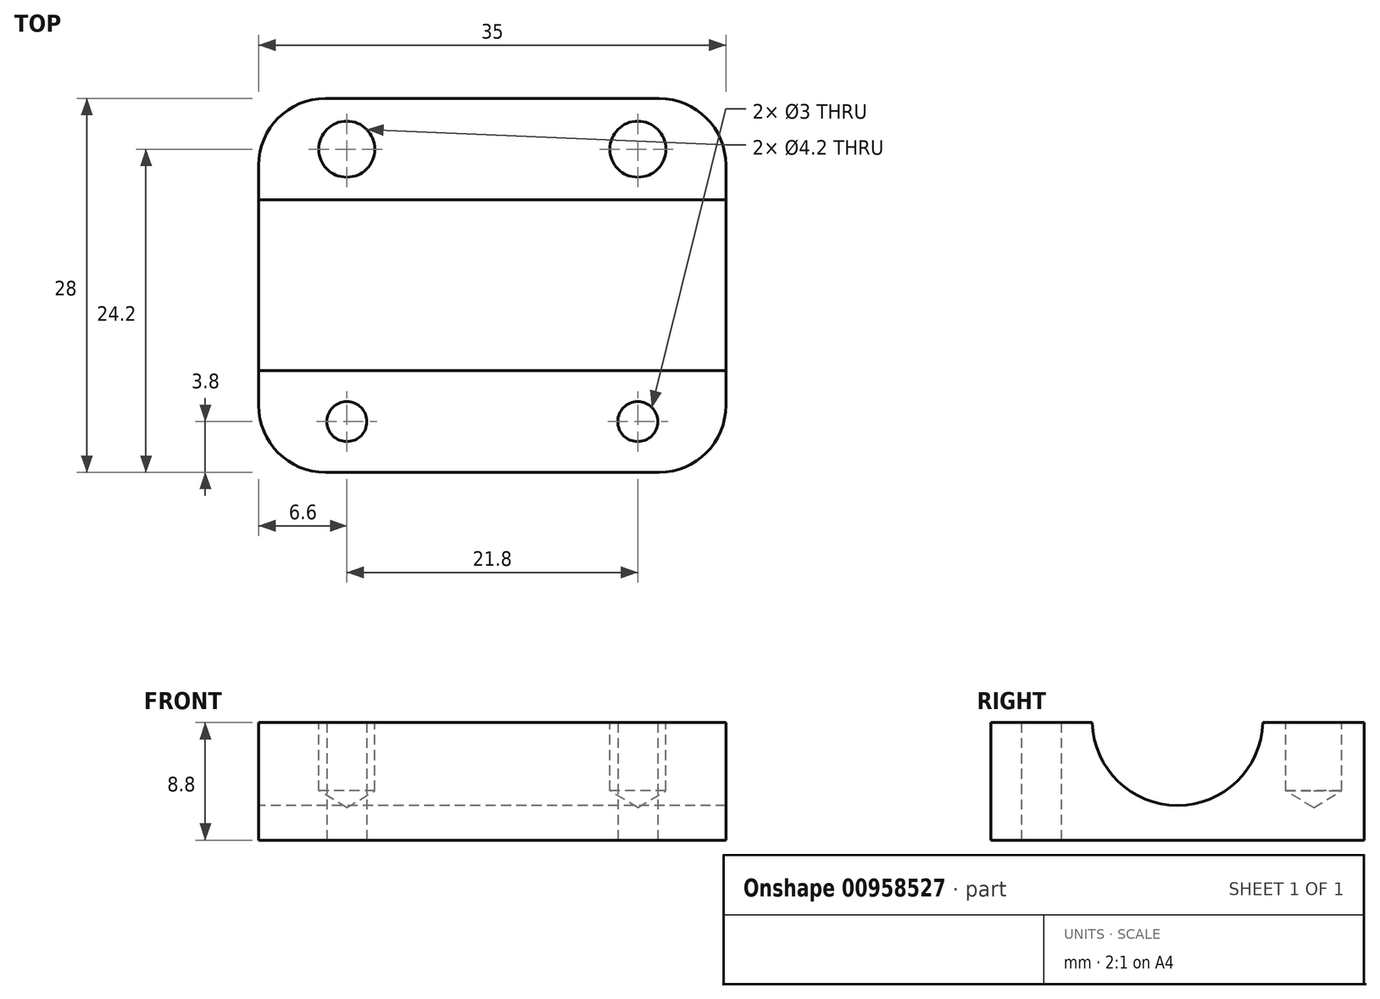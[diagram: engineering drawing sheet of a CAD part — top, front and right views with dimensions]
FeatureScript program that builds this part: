
annotation { "Feature Type Name" : "Feature", "Feature Type Description" : "" }
export const myFeature = defineFeature(function(context is Context, id is Id, definition is map)
    precondition{}
    {
        {
            var Q0;
            Q0=qCreatedBy(makeId("Top.planeOp"),FACE);
            var sketch = newSketch(context, id + "F0", { "sketchPlane" : qUnion([Q0])});
            skLineSegment(sketch, "E0.bottom", {"start": v(17.5, -14) * mm, "end": v(-17.5, -14) * mm});
            skLineSegment(sketch, "E0.top", {"start": v(17.5, 14) * mm, "end": v(-17.5, 14) * mm});
            skLineSegment(sketch, "E0.left", {"start": v(17.5, -14) * mm, "end": v(17.5, 14) * mm});
            skLineSegment(sketch, "E0.right", {"start": v(-17.5, -14) * mm, "end": v(-17.5, 14) * mm});
            skPoint(sketch, "E0.middle", {"position": v(0, 0) * mm});
            skPoint(sketch, "E1", {"position": v(10.9, -10.2) * mm});
            skPoint(sketch, "E2.1.0.0", {"position": v(-10.9, -10.2) * mm});
            skLineSegment(sketch, "E2.direction1", {"start": v(10.9, -10.2) * mm, "end": v(-10.9, -10.2) * mm, "construction": true});
            skSolve(sketch);
        }
        {
            var Q0;
            Q0=makeQuery(id+"F0.imprint","IMPRINT",FACE,{"disambiguationData":[TD([[makeQuery(id+"F0.imprint","IMPRINT",EDGE,{"derivedFrom":sQuery(id+"F0.wireOp",EDGE,"E0.bottom")}),-1.0]])]});
            extrude(context, id + "F1", {"entities" : qUnion([Q0]), "depth" : 14 * mm, "offsetDistance" : 25 * mm});
        }
        {
            var Q0;
            Q0=makeQuery(id+"F1.opExtrude","SWEPT_FACE",FACE,{"disambiguationData":[OSD([sQuery(id+"F0.wireOp",EDGE,"E0.right")])]});
            var sketch = newSketch(context, id + "F2", { "sketchPlane" : qUnion([Q0])});
            skPoint(sketch, "E3", {"position": v(0, 7) * mm});
            skPoint(sketch, "E3.positionSnap0", {"position": v(0, 14) * mm});
            skPoint(sketch, "E3.positionSnap1", {"position": v(-14, 7) * mm});
            skLineSegment(sketch, "E4", {"start": v(14, 7) * mm, "end": v(-14, 7) * mm});
            skSolve(sketch);
        }
        {
            var Q0;
            Q0=sQuery(id+"F2.wireOp",VERTEX,"E3");
            var Q1;
            Q1=makeQuery(id+"F1.opExtrude","SWEPT_BODY",BODY,{"disambiguationData":[OSD([sQuery(id+"F0.wireOp",EDGE,"E0.bottom"),sQuery(id+"F0.wireOp",EDGE,"E0.top"),sQuery(id+"F0.wireOp",EDGE,"E0.left"),sQuery(id+"F0.wireOp",EDGE,"E0.right")])]});
            hole(context, id + "F3", {"style" : HoleStyle.SIMPLE, "endStyle" : HoleEndStyle.THROUGH, "holeDiameter" : 12.8 * mm, "majorDiameter" : 5 * mm, "isTappedThrough" : true, "tappedDepth" : 12 * mm, "tapClearance" : 3, "startFromSketch" : true, "locations" : qUnion([Q0]), "scope" : qUnion([Q1])});
        }
        {
            var Q0;
            Q0=makeQuery(id+"F1.opExtrude","CAP_FACE",FACE,{"disambiguationData":[OSD([sQuery(id+"F0.wireOp",EDGE,"E0.bottom"),sQuery(id+"F0.wireOp",EDGE,"E0.top"),sQuery(id+"F0.wireOp",EDGE,"E0.left"),sQuery(id+"F0.wireOp",EDGE,"E0.right")])],"isStart":false});
            extrude(context, id + "F4", {"entities" : qUnion([Q0]), "operationType" : NewBodyOperationType.REMOVE, "oppositeDirection" : true, "depth" : 7.2 * mm, "offsetDistance" : 25 * mm});
        }
        {
            var Q0;
            Q0=makeQuery(id+"F1.opExtrude","SWEPT_EDGE",EDGE,{"disambiguationData":[OSD([sQuery(id+"F0.wireOp",EDGE,"E0.top"),sQuery(id+"F0.wireOp",EDGE,"E0.left")])]});
            var Q1;
            Q1=makeQuery(id+"F1.opExtrude","SWEPT_EDGE",EDGE,{"disambiguationData":[OSD([sQuery(id+"F0.wireOp",EDGE,"E0.top"),sQuery(id+"F0.wireOp",EDGE,"E0.right")])]});
            var Q2;
            Q2=makeQuery(id+"F1.opExtrude","SWEPT_EDGE",EDGE,{"disambiguationData":[OSD([sQuery(id+"F0.wireOp",EDGE,"E0.bottom"),sQuery(id+"F0.wireOp",EDGE,"E0.left")])]});
            var Q3;
            Q3=makeQuery(id+"F1.opExtrude","SWEPT_EDGE",EDGE,{"disambiguationData":[OSD([sQuery(id+"F0.wireOp",EDGE,"E0.bottom"),sQuery(id+"F0.wireOp",EDGE,"E0.right")])]});
            fillet(context, id + "F5", {"entities" : qUnion([Q0, Q1, Q2, Q3]), "radius" : 5 * mm, "tangentPropagation" : true, "allowEdgeOverflow" : false});
        }
        {
            var Q0;
            Q0=sQuery(id+"F0.wireOp",VERTEX,"E1");
            var Q1;
            Q1=sQuery(id+"F0.wireOp",VERTEX,"E2.1.0.0");
            var Q2;
            Q2=makeQuery(id+"F1.opExtrude","SWEPT_BODY",BODY,{"disambiguationData":[OSD([sQuery(id+"F0.wireOp",EDGE,"E0.bottom"),sQuery(id+"F0.wireOp",EDGE,"E0.top"),sQuery(id+"F0.wireOp",EDGE,"E0.left"),sQuery(id+"F0.wireOp",EDGE,"E0.right")])]});
            hole(context, id + "F6", {"style" : HoleStyle.SIMPLE, "endStyle" : HoleEndStyle.THROUGH, "oppositeDirection" : true, "holeDiameter" : 3 * mm, "majorDiameter" : 5 * mm, "isTappedThrough" : true, "tappedDepth" : 12 * mm, "tapClearance" : 3, "startFromSketch" : true, "locations" : qUnion([Q0, Q1]), "scope" : qUnion([Q2])});
        }
        {
            var Q0;
            {var subQ0=sQuery(id+"F0.wireOp",EDGE,"E0.top");var subQ1=sQuery(id+"F0.wireOp",EDGE,"E0.left");var subQ2=sQuery(id+"F0.wireOp",EDGE,"E0.right");Q0=makeQuery(id+"F4.boolean.opBoolean","COPY",FACE,{"disambiguationData":[TD([makeQuery(id+"F1.opExtrude","SWEPT_FACE",FACE,{"disambiguationData":[OSD([subQ0])]})])],"derivedFrom":makeQuery(id+"F4.opExtrude","CAP_FACE",FACE,{"disambiguationData":[OSD([sQuery(id+"F0.wireOp",EDGE,"E0.bottom"),subQ0,subQ1,subQ2])],"isStart":false})});}
            var sketch = newSketch(context, id + "F7", { "sketchPlane" : qUnion([Q0])});
            skPoint(sketch, "E5", {"position": v(-10.9, 10.2) * mm});
            skPoint(sketch, "E6.1.0.0", {"position": v(10.9, 10.2) * mm});
            skLineSegment(sketch, "E6.direction1", {"start": v(-10.9, 10.2) * mm, "end": v(10.9, 10.2) * mm, "construction": true});
            skSolve(sketch);
        }
        {
            var Q0;
            Q0=sQuery(id+"F7.wireOp",VERTEX,"E5");
            var Q1;
            Q1=sQuery(id+"F7.wireOp",VERTEX,"E6.1.0.0");
            var Q2;
            Q2=makeQuery(id+"F1.opExtrude","SWEPT_BODY",BODY,{"disambiguationData":[OSD([sQuery(id+"F0.wireOp",EDGE,"E0.bottom"),sQuery(id+"F0.wireOp",EDGE,"E0.top"),sQuery(id+"F0.wireOp",EDGE,"E0.left"),sQuery(id+"F0.wireOp",EDGE,"E0.right")])]});
            hole(context, id + "F8", {"style" : HoleStyle.SIMPLE, "endStyle" : HoleEndStyle.BLIND, "holeDiameter" : 4.2 * mm, "majorDiameter" : 5 * mm, "holeDepth" : 5.1 * mm, "isTappedThrough" : true, "tappedDepth" : 12 * mm, "tapClearance" : 3, "startFromSketch" : true, "locations" : qUnion([Q0, Q1]), "scope" : qUnion([Q2])});
        }
        {
            var Q0;
            Q0=makeQuery(id+"F1.opExtrude","CAP_FACE",FACE,{"disambiguationData":[OSD([sQuery(id+"F0.wireOp",EDGE,"E0.bottom"),sQuery(id+"F0.wireOp",EDGE,"E0.top"),sQuery(id+"F0.wireOp",EDGE,"E0.left"),sQuery(id+"F0.wireOp",EDGE,"E0.right")])],"isStart":true});
            extrude(context, id + "F9", {"entities" : qUnion([Q0]), "operationType" : NewBodyOperationType.ADD, "depth" : 2 * mm, "offsetDistance" : 25 * mm});
        }
    });
